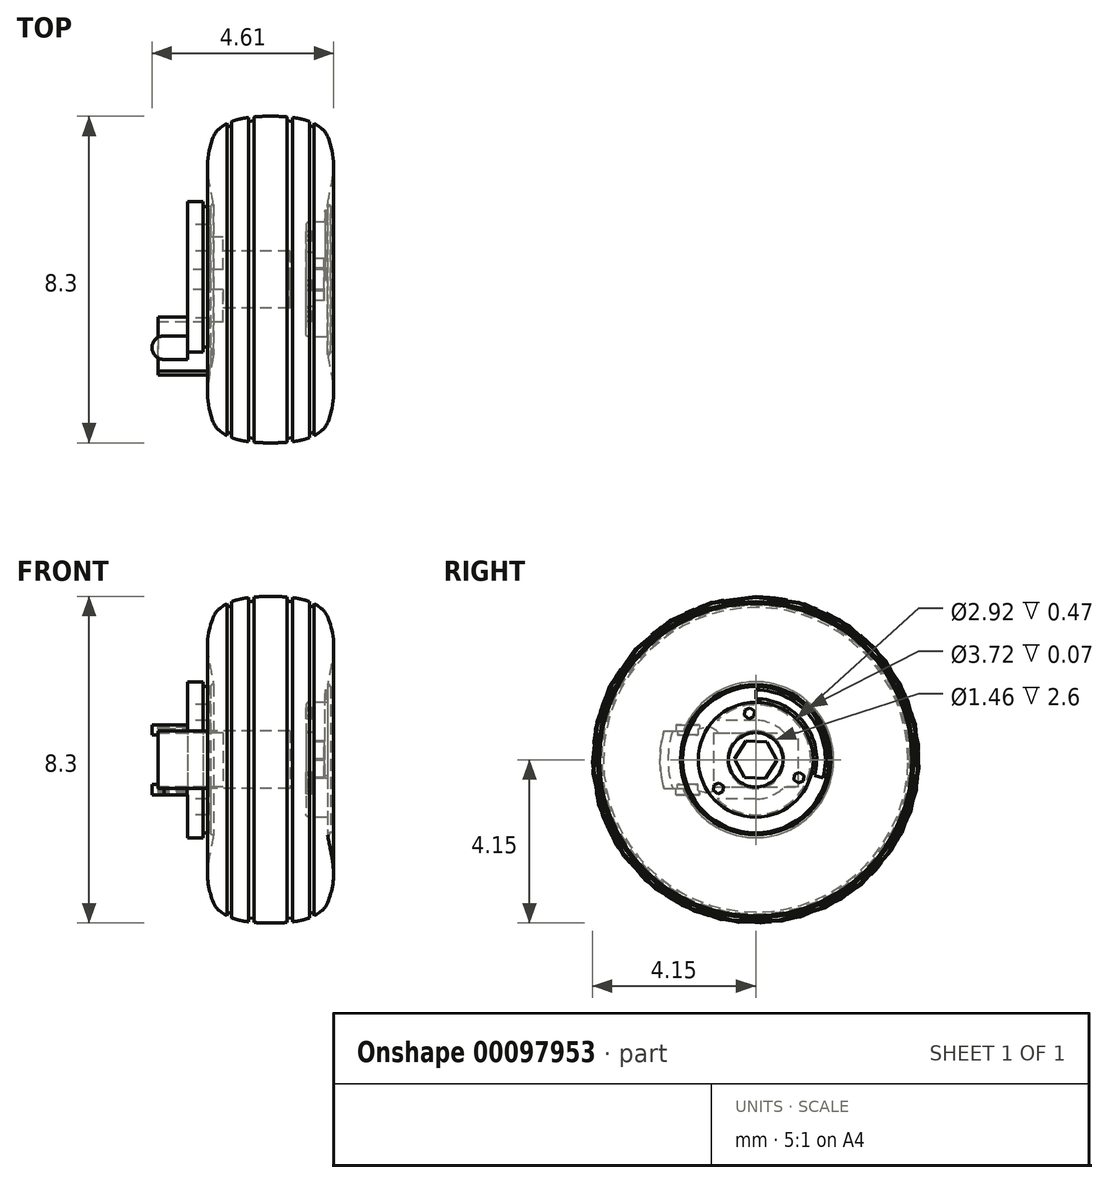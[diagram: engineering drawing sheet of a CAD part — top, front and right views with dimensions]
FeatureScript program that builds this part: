
annotation { "Feature Type Name" : "Feature", "Feature Type Description" : "" }
export const myFeature = defineFeature(function(context is Context, id is Id, definition is map)
    precondition{}
    {
        {
            var Q0;
            Q0=qCreatedBy(makeId("Front.planeOp"),FACE);
            var sketch = newSketch(context, id + "F0", { "sketchPlane" : qUnion([Q0])});
            skLineSegment(sketch, "E0.bottom", {"start": v(0, 0) * mm, "end": v(1.1, 0) * mm});
            skLineSegment(sketch, "E0.top", {"start": v(0.98, 0.7) * mm, "end": v(1.1, 0.7) * mm});
            skLineSegment(sketch, "E0.right", {"start": v(1.11, 0) * mm, "end": v(1.11, 0.7) * mm});
            skLineSegment(sketch, "E1", {"start": v(0.9, 0.77) * mm, "end": v(0.9, 1.38) * mm});
            skLineSegment(sketch, "E2", {"start": v(0.98, 1.46) * mm, "end": v(1.27, 1.46) * mm});
            skLineSegment(sketch, "E3", {"start": v(1.45, 1.64) * mm, "end": v(1.45, 1.86) * mm});
            skLineSegment(sketch, "E4", {"start": v(1.45, 1.91) * mm, "end": v(1.45, 1.91) * mm});
            skLineSegment(sketch, "E5", {"start": v(1.52, 1.91) * mm, "end": v(1.52, 1.91) * mm});
            skLineSegment(sketch, "E6", {"start": v(1.47, 1.91) * mm, "end": v(1.45, 1.91) * mm});
            skPoint(sketch, "E7.orphan", {"position": v(0, 1.46) * mm});
            skPoint(sketch, "E8.visualSharp", {"position": v(1.45, 1.46) * mm});
            skPoint(sketch, "E9.visualSharp", {"position": v(0.9, 1.46) * mm});
            skArc(sketch, "E9.filletArc", {"start": v(0.98, 1.46) * mm, "mid": v(0.92, 1.44) * mm, "end": v(0.9, 1.38) * mm});
            skArc(sketch, "E10.filletArc", {"start": v(0.9, 0.77) * mm, "mid": v(0.92, 0.71) * mm, "end": v(0.98, 0.7) * mm});
            skPoint(sketch, "E11.visualSharp", {"position": v(1.52, 1.91) * mm});
            skArc(sketch, "E11.filletArc", {"start": v(1.52, 1.86) * mm, "mid": v(1.5, 1.9) * mm, "end": v(1.47, 1.91) * mm});
            skLineSegment(sketch, "E12", {"start": v(-0.76, 4.15) * mm, "end": v(0, 4.15) * mm, "construction": true});
            skLineSegment(sketch, "E13", {"start": v(1.6, 4.08) * mm, "end": v(1.6, 0.98) * mm, "construction": true});
            skFitSpline(sketch, "E14", {"points": [v(0, 4.15) * mm, v(1.28, 3.85) * mm, v(1.4, 3.73) * mm, v(1.6, 2.99) * mm, v(1.45, 1.91) * mm], "startDerivative": vector(8.32, 0) * mm, "endDerivative": vector(-0.59, -3.7) * mm});
            skLineSegment(sketch, "E15", {"start": v(0, 4.15) * mm, "end": v(1.72, 4.15) * mm, "construction": true});
            skLineSegment(sketch, "E16", {"start": v(0.42, 4.03) * mm, "end": v(0.56, 4.02) * mm});
            skLineSegment(sketch, "E17", {"start": v(0.99, 3.92) * mm, "end": v(1.1, 3.87) * mm});
            skLineSegment(sketch, "E18", {"start": v(0.42, 4.03) * mm, "end": v(0.42, 4.13) * mm});
            skLineSegment(sketch, "E19", {"start": v(0.56, 4.02) * mm, "end": v(0.56, 4.12) * mm});
            skLineSegment(sketch, "E20", {"start": v(0.99, 3.92) * mm, "end": v(0.99, 4.02) * mm});
            skLineSegment(sketch, "E21", {"start": v(1.1, 3.87) * mm, "end": v(1.1, 3.97) * mm});
            skLineSegment(sketch, "E22", {"start": v(1.52, 1.86) * mm, "end": v(1.45, 1.86) * mm});
            skLineSegment(sketch, "E23", {"start": v(1.27, 1.46) * mm, "end": v(1.45, 1.46) * mm});
            skLineSegment(sketch, "E24", {"start": v(1.45, 1.46) * mm, "end": v(1.45, 1.64) * mm});
            skLineSegment(sketch, "E25.MirrorCS", {"start": v(-1.11, 0) * mm, "end": v(-1.11, 0.7) * mm, "construction": true});
            skLineSegment(sketch, "E26.MirrorCS", {"start": v(-0.98, 0.7) * mm, "end": v(-1.1, 0.7) * mm, "construction": true});
            skArc(sketch, "E27.MirrorCS", {"start": v(-0.9, 0.77) * mm, "mid": v(-0.92, 0.71) * mm, "end": v(-0.98, 0.7) * mm, "construction": true});
            skLineSegment(sketch, "E28.MirrorCS", {"start": v(-0.9, 0.77) * mm, "end": v(-0.9, 1.38) * mm, "construction": true});
            skArc(sketch, "E29.MirrorCS", {"start": v(-1.52, 1.86) * mm, "mid": v(-1.5, 1.9) * mm, "end": v(-1.47, 1.91) * mm});
            skLineSegment(sketch, "E30.MirrorCS", {"start": v(-1.47, 1.91) * mm, "end": v(-1.45, 1.91) * mm});
            skLineSegment(sketch, "E31", {"start": v(-2.1, 1.98) * mm, "end": v(-2.1, 1.4) * mm});
            skLineSegment(sketch, "E32", {"start": v(-2.1, 1.98) * mm, "end": v(-1.71, 1.98) * mm});
            skLineSegment(sketch, "E33", {"start": v(-2.1, 1.4) * mm, "end": v(-1.61, 1.4) * mm});
            skPoint(sketch, "E34.orphan", {"position": v(-2.1, 0.82) * mm});
            skLineSegment(sketch, "E35", {"start": v(-1.61, 0.73) * mm, "end": v(0.49, 0.73) * mm});
            skLineSegment(sketch, "E36", {"start": v(0.49, 0) * mm, "end": v(0.49, 0.96) * mm});
            skLineSegment(sketch, "E37", {"start": v(-0.97, 1.4) * mm, "end": v(-0.97, 0.96) * mm, "construction": true});
            skLineSegment(sketch, "E38", {"start": v(-1.71, 1.98) * mm, "end": v(-1.71, 1.86) * mm});
            skLineSegment(sketch, "E39", {"start": v(-1.52, 1.86) * mm, "end": v(-1.71, 1.86) * mm});
            skLineSegment(sketch, "E40", {"start": v(-2.64, 1.27) * mm, "end": v(-2.64, -0.73) * mm, "construction": true});
            skLineSegment(sketch, "E41", {"start": v(-1.61, 1.4) * mm, "end": v(-1.61, 0.73) * mm});
            skPoint(sketch, "E42.orphan", {"position": v(0, 0.73) * mm});
            skLineSegment(sketch, "E43", {"start": v(-1.61, 1.4) * mm, "end": v(-0.97, 1.4) * mm, "construction": true});
            skLineSegment(sketch, "E44", {"start": v(0, 0.73) * mm, "end": v(0, 5.2) * mm, "construction": true});
            skLineSegment(sketch, "E45.MirrorCS", {"start": v(-1.1, 3.87) * mm, "end": v(-1.1, 3.97) * mm});
            skLineSegment(sketch, "E46.MirrorCS", {"start": v(-0.99, 3.92) * mm, "end": v(-1.1, 3.87) * mm});
            skLineSegment(sketch, "E47.MirrorCS", {"start": v(-0.99, 3.92) * mm, "end": v(-0.99, 4.02) * mm});
            skFitSpline(sketch, "E48.MirrorCS", {"points": [v(0, 4.15) * mm, v(-1.28, 3.85) * mm, v(-1.4, 3.73) * mm, v(-1.6, 2.99) * mm, v(-1.45, 1.91) * mm], "startDerivative": vector(-8.32, 0) * mm, "endDerivative": vector(0.59, -3.7) * mm});
            skLineSegment(sketch, "E49.MirrorCS", {"start": v(-0.42, 4.03) * mm, "end": v(-0.56, 4.02) * mm});
            skLineSegment(sketch, "E50.MirrorCS", {"start": v(-0.42, 4.03) * mm, "end": v(-0.42, 4.13) * mm});
            skLineSegment(sketch, "E51.MirrorCS", {"start": v(-0.56, 4.02) * mm, "end": v(-0.56, 4.12) * mm});
            skLineSegment(sketch, "E52.MirrorCS", {"start": v(-1.52, 1.91) * mm, "end": v(-1.52, 1.91) * mm});
            skFitSpline(sketch, "E53.MirrorCS", {"points": [v(0, 4.15) * mm, v(-1.28, 3.85) * mm, v(-1.4, 3.73) * mm, v(-1.6, 2.99) * mm, v(-1.45, 1.91) * mm], "startDerivative": vector(-8.32, 0) * mm, "endDerivative": vector(0.59, -3.7) * mm});
            skSolve(sketch);
        }
        {
            var Q0;
            Q0=makeQuery(id+"F0.imprint","IMPRINT",FACE,{"disambiguationData":[TD([[makeQuery(id+"F0.imprint","IMPRINT",EDGE,{"derivedFrom":sQuery(id+"F0.wireOp",EDGE,"E0.top")}),-1.0]])]});
            var Q1;
            Q1=sQuery(id+"F0.wireOp",EDGE,"E25.MirrorCS");
            var Q2;
            Q2=sQuery(id+"F0.wireOp",EDGE,"E28.MirrorCS");
            var Q3;
            Q3=sQuery(id+"F0.wireOp",EDGE,"E27.MirrorCS");
            var Q4;
            Q4=sQuery(id+"F0.wireOp",EDGE,"E26.MirrorCS");
            var Q5;
            Q5=sQuery(id+"F0.wireOp",EDGE,"E0.bottom");
            revolve(context, id + "F1", {"entities" : qUnion([Q0]), "surfaceEntities" : qUnion([Q1, Q2, Q3, Q4]), "axis" : qUnion([Q5]), "revolveType" : RevolveType.FULL});
        }
        {
            var Q0;
            Q0=makeQuery(id+"F1.opRevolve","SWEPT_FACE",FACE,{"disambiguationData":[OSD([sQuery(id+"F0.wireOp",EDGE,"E31")])]});
            var sketch = newSketch(context, id + "F2", { "sketchPlane" : qUnion([Q0])});
            skArc(sketch, "E54", {"start": v(0, 1) * mm, "mid": v(-1, 0) * mm, "end": v(0, -1) * mm});
            skLineSegment(sketch, "E55", {"start": v(0, 1) * mm, "end": v(0.98, 1) * mm});
            skLineSegment(sketch, "E56", {"start": v(0, -1) * mm, "end": v(0.98, -1) * mm});
            skArc(sketch, "E57", {"start": v(0.98, -1) * mm, "mid": v(1.4, 0) * mm, "end": v(0.98, 1) * mm});
            skCircle(sketch, "E58", {"center": v(0, 0) * mm, "radius": 0.73 * mm});
            skSolve(sketch);
        }
        {
            var Q0;
            Q0=qSketchRegion(id+"F2",true);
            var Q1;
            Q1=makeQuery(id+"F1.opRevolve","SWEPT_FACE",FACE,{"disambiguationData":[OSD([sQuery(id+"F0.wireOp",EDGE,"E41")])]});
            extrude(context, id + "F3", {"entities" : qUnion([Q0]), "operationType" : NewBodyOperationType.ADD, "endBound" : BoundingType.UP_TO_SURFACE, "oppositeDirection" : true, "endBoundEntityFace" : qUnion([Q1]), "depth" : 25 * mm});
        }
        {
            var Q0;
            Q0=makeQuery(id+"F3.boolean.opBoolean","MERGE",FACE,{"derivedFrom":[makeQuery(id+"F1.opRevolve","SWEPT_FACE",FACE,{"disambiguationData":[OSD([sQuery(id+"F0.wireOp",EDGE,"E31")])]}),makeQuery(id+"F3.opExtrude","CAP_FACE",FACE,{"disambiguationData":[OSD([sQuery(id+"F2.wireOp",EDGE,"E54"),sQuery(id+"F2.wireOp",EDGE,"E55"),sQuery(id+"F2.wireOp",EDGE,"E56"),sQuery(id+"F2.wireOp",EDGE,"E58"),sQuery(id+"F2.wireOp",EDGE,"E57")])],"isStart":true})]});
            var sketch = newSketch(context, id + "F4", { "sketchPlane" : qUnion([Q0])});
            skLineSegment(sketch, "E59.bottom", {"start": v(1.08, 0.68) * mm, "end": v(-1.08, 0.69) * mm});
            skLineSegment(sketch, "E59.top", {"start": v(1.08, -0.69) * mm, "end": v(-1.08, -0.68) * mm});
            skLineSegment(sketch, "E59.left", {"start": v(1.08, 0.68) * mm, "end": v(1.08, -0.69) * mm});
            skLineSegment(sketch, "E59.right", {"start": v(-1.08, 0.69) * mm, "end": v(-1.08, -0.68) * mm});
            skPoint(sketch, "E59.middle", {"position": v(0, 0) * mm});
            skSolve(sketch);
        }
        {
            var Q0;
            Q0=qSketchRegion(id+"F4",true);
            extrude(context, id + "F5", {"entities" : qUnion([Q0]), "operationType" : NewBodyOperationType.REMOVE, "oppositeDirection" : true, "depth" : 0.9 * mm});
        }
        {
            var Q0;
            Q0=makeQuery(id+"F3.boolean.opBoolean","MERGE",FACE,{"derivedFrom":[makeQuery(id+"F1.opRevolve","SWEPT_FACE",FACE,{"disambiguationData":[OSD([sQuery(id+"F0.wireOp",EDGE,"E31")])]}),makeQuery(id+"F3.opExtrude","CAP_FACE",FACE,{"disambiguationData":[OSD([sQuery(id+"F2.wireOp",EDGE,"E54"),sQuery(id+"F2.wireOp",EDGE,"E55"),sQuery(id+"F2.wireOp",EDGE,"E56"),sQuery(id+"F2.wireOp",EDGE,"E58"),sQuery(id+"F2.wireOp",EDGE,"E57")])],"isStart":true})]});
            var sketch = newSketch(context, id + "F6", { "sketchPlane" : qUnion([Q0])});
            skLineSegment(sketch, "E60", {"start": v(2.33, 0.73) * mm, "end": v(2.33, -0.73) * mm, "construction": true});
            skLineSegment(sketch, "E61", {"start": v(0, 0) * mm, "end": v(2.43, 0) * mm, "construction": true});
            skArc(sketch, "E62", {"start": v(2.43, 0) * mm, "mid": v(2.4, 0.37) * mm, "end": v(2.33, 0.73) * mm});
            skLineSegment(sketch, "E63", {"start": v(2.33, 0.73) * mm, "end": v(1.68, 0.73) * mm});
            skLineSegment(sketch, "E64", {"start": v(2.65, 0.83) * mm, "end": v(-0.85, 0.83) * mm, "construction": true});
            skLineSegment(sketch, "E65", {"start": v(0.89, 2.3) * mm, "end": v(0.9, -2.15) * mm, "construction": true});
            skLineSegment(sketch, "E66", {"start": v(1.23, 1.18) * mm, "end": v(1.23, 0.25) * mm, "construction": true});
            skLineSegment(sketch, "E67", {"start": v(1.57, 0.49) * mm, "end": v(0.7, 0.49) * mm, "construction": true});
            skArc(sketch, "E68", {"start": v(1.31, 0.82) * mm, "mid": v(1.11, 0.8) * mm, "end": v(0.95, 0.68) * mm});
            skLineSegment(sketch, "E69", {"start": v(1.68, 0.73) * mm, "end": v(1.27, 0.83) * mm});
            skLineSegment(sketch, "E70", {"start": v(0.95, 0.68) * mm, "end": v(1.08, 0.68) * mm});
            skLineSegment(sketch, "E71", {"start": v(1.08, 0.68) * mm, "end": v(1.08, 0) * mm});
            skLineSegment(sketch, "E72", {"start": v(1.08, 0) * mm, "end": v(2.43, 0) * mm});
            skArc(sketch, "E73.MirrorCS", {"start": v(2.43, 0) * mm, "mid": v(2.4, -0.37) * mm, "end": v(2.33, -0.73) * mm});
            skLineSegment(sketch, "E74.MirrorCS", {"start": v(2.33, -0.73) * mm, "end": v(1.68, -0.73) * mm});
            skLineSegment(sketch, "E75.MirrorCS", {"start": v(1.68, -0.73) * mm, "end": v(1.27, -0.83) * mm});
            skArc(sketch, "E76.MirrorCS", {"start": v(1.31, -0.82) * mm, "mid": v(1.11, -0.8) * mm, "end": v(0.95, -0.68) * mm});
            skLineSegment(sketch, "E77.MirrorCS", {"start": v(0.95, -0.68) * mm, "end": v(1.08, -0.68) * mm});
            skLineSegment(sketch, "E78.MirrorCS", {"start": v(1.08, -0.68) * mm, "end": v(1.08, 0) * mm});
            skSolve(sketch);
        }
        {
            var Q0;
            Q0=qSketchRegion(id+"F6",true);
            extrude(context, id + "F7", {"entities" : qUnion([Q0]), "operationType" : NewBodyOperationType.ADD, "depth" : 0.75 * mm, "hasSecondDirection" : true, "secondDirectionOppositeDirection" : true, "secondDirectionDepth" : 0.6 * mm});
        }
        {
            var Q0;
            Q0=makeQuery(id+"F7.opExtrude","SWEPT_FACE",FACE,{"disambiguationData":[OSD([sQuery(id+"F6.wireOp",EDGE,"E63")])]});
            var sketch = newSketch(context, id + "F8", { "sketchPlane" : qUnion([Q0])});
            skLineSegment(sketch, "E79", {"start": v(-2.7, -1.43) * mm, "end": v(-2.7, -2.03) * mm, "construction": true});
            skArc(sketch, "E80", {"start": v(-2.7, -1.43) * mm, "mid": v(-3, -1.73) * mm, "end": v(-2.7, -2.03) * mm});
            skLineSegment(sketch, "E81", {"start": v(-2.1, -2.03) * mm, "end": v(-2.1, -1.43) * mm});
            skLineSegment(sketch, "E82", {"start": v(-2.7, -1.43) * mm, "end": v(-2.1, -1.43) * mm});
            skLineSegment(sketch, "E83", {"start": v(-2.7, -2.03) * mm, "end": v(-2.1, -2.03) * mm});
            skSolve(sketch);
        }
        {
            var Q0;
            Q0=qSketchRegion(id+"F8",true);
            extrude(context, id + "F9", {"entities" : qUnion([Q0]), "operationType" : NewBodyOperationType.ADD, "depth" : 0.16 * mm, "hasSecondDirection" : true, "secondDirectionOppositeDirection" : true, "secondDirectionDepth" : 0.1 * mm});
        }
        {
            var Q0;
            Q0=makeQuery(id+"F7.opExtrude","SWEPT_FACE",FACE,{"disambiguationData":[OSD([sQuery(id+"F6.wireOp",EDGE,"E74.MirrorCS")])]});
            var sketch = newSketch(context, id + "F10", { "sketchPlane" : qUnion([Q0])});
            skArc(sketch, "E84", {"start": v(-2.7, 2.03) * mm, "mid": v(-3.01, 1.73) * mm, "end": v(-2.7, 1.43) * mm});
            skLineSegment(sketch, "E85", {"start": v(-2.7, 1.43) * mm, "end": v(-2.12, 1.43) * mm});
            skLineSegment(sketch, "E86", {"start": v(-2.12, 1.43) * mm, "end": v(-2.12, 2.03) * mm});
            skLineSegment(sketch, "E87", {"start": v(-2.72, 2.03) * mm, "end": v(-2.12, 2.03) * mm});
            skSolve(sketch);
        }
        {
            var Q0;
            Q0=qSketchRegion(id+"F10",true);
            extrude(context, id + "F11", {"entities" : qUnion([Q0]), "operationType" : NewBodyOperationType.ADD, "depth" : 0.16 * mm, "hasSecondDirection" : true, "secondDirectionOppositeDirection" : true, "secondDirectionDepth" : 0.1 * mm});
        }
        {
            var Q0;
            Q0=makeQuery(id+"F1.opRevolve","SWEPT_FACE",FACE,{"disambiguationData":[OSD([sQuery(id+"F0.wireOp",EDGE,"E0.right")])]});
            var sketch = newSketch(context, id + "F12", { "sketchPlane" : qUnion([Q0])});
            skCircle(sketch, "E88.cCircle", {"center": v(0, 0) * mm, "radius": 0.47 * mm, "construction": true});
            skLineSegment(sketch, "E88.0", {"start": v(0.29, 0.45) * mm, "end": v(0.54, -0.02) * mm});
            skLineSegment(sketch, "E88.1", {"start": v(0.54, -0.02) * mm, "end": v(0.25, -0.48) * mm});
            skLineSegment(sketch, "E88.2", {"start": v(0.25, -0.48) * mm, "end": v(-0.29, -0.45) * mm});
            skLineSegment(sketch, "E88.3", {"start": v(-0.29, -0.45) * mm, "end": v(-0.54, 0.02) * mm});
            skLineSegment(sketch, "E88.4", {"start": v(-0.54, 0.02) * mm, "end": v(-0.25, 0.48) * mm});
            skLineSegment(sketch, "E88.5", {"start": v(-0.25, 0.48) * mm, "end": v(0.29, 0.45) * mm});
            skPoint(sketch, "E88.0.midPoint", {"position": v(0.41, 0.22) * mm});
            skSolve(sketch);
        }
        {
            var Q0;
            Q0=qSketchRegion(id+"F12",true);
            extrude(context, id + "F13", {"entities" : qUnion([Q0]), "operationType" : NewBodyOperationType.ADD, "depth" : 0.25 * mm});
        }
        {
            var Q0;
            Q0=makeQuery(id+"F1.opRevolve","SWEPT_FACE",FACE,{"disambiguationData":[OSD([sQuery(id+"F0.wireOp",EDGE,"E1")])]});
            var sketch = newSketch(context, id + "F14", { "sketchPlane" : qUnion([Q0])});
            skPoint(sketch, "E89.center", {"position": v(0, 0) * mm});
            skCircle(sketch, "E90.cCircle", {"center": v(-0.16, 1.18) * mm, "radius": 0.12 * mm, "construction": true});
            skLineSegment(sketch, "E90.0", {"start": v(-0.28, 1.12) * mm, "end": v(-0.27, 1.26) * mm});
            skLineSegment(sketch, "E90.1", {"start": v(-0.27, 1.26) * mm, "end": v(-0.14, 1.32) * mm});
            skLineSegment(sketch, "E90.2", {"start": v(-0.14, 1.32) * mm, "end": v(-0.03, 1.24) * mm});
            skLineSegment(sketch, "E90.3", {"start": v(-0.03, 1.24) * mm, "end": v(-0.04, 1.1) * mm});
            skLineSegment(sketch, "E90.4", {"start": v(-0.04, 1.1) * mm, "end": v(-0.17, 1.04) * mm});
            skLineSegment(sketch, "E90.5", {"start": v(-0.17, 1.04) * mm, "end": v(-0.28, 1.12) * mm});
            skPoint(sketch, "E90.0.midPoint", {"position": v(-0.27, 1.19) * mm});
            skLineSegment(sketch, "E91", {"start": v(0, 0) * mm, "end": v(-0.16, 1.18) * mm, "construction": true});
            skLineSegment(sketch, "E92.1.0", {"start": v(-0.83, -0.8) * mm, "end": v(-0.96, -0.86) * mm});
            skLineSegment(sketch, "E92.1.1", {"start": v(-0.96, -0.86) * mm, "end": v(-1.07, -0.78) * mm});
            skLineSegment(sketch, "E92.1.2", {"start": v(-1.07, -0.78) * mm, "end": v(-1.06, -0.65) * mm});
            skLineSegment(sketch, "E92.1.3", {"start": v(-1.06, -0.65) * mm, "end": v(-0.93, -0.59) * mm});
            skLineSegment(sketch, "E92.1.4", {"start": v(-0.93, -0.59) * mm, "end": v(-0.82, -0.67) * mm});
            skLineSegment(sketch, "E92.1.5", {"start": v(-0.82, -0.67) * mm, "end": v(-0.83, -0.8) * mm});
            skCircle(sketch, "E92.1.6", {"center": v(-0.94, -0.72) * mm, "radius": 0.12 * mm, "construction": true});
            skLineSegment(sketch, "E92.2.0", {"start": v(1.11, -0.32) * mm, "end": v(1.22, -0.4) * mm});
            skLineSegment(sketch, "E92.2.1", {"start": v(1.22, -0.4) * mm, "end": v(1.21, -0.53) * mm});
            skLineSegment(sketch, "E92.2.2", {"start": v(1.21, -0.53) * mm, "end": v(1.09, -0.6) * mm});
            skLineSegment(sketch, "E92.2.3", {"start": v(1.09, -0.6) * mm, "end": v(0.97, -0.51) * mm});
            skLineSegment(sketch, "E92.2.4", {"start": v(0.97, -0.51) * mm, "end": v(0.99, -0.38) * mm});
            skLineSegment(sketch, "E92.2.5", {"start": v(0.99, -0.38) * mm, "end": v(1.11, -0.32) * mm});
            skCircle(sketch, "E92.2.6", {"center": v(1.1, -0.46) * mm, "radius": 0.12 * mm, "construction": true});
            skSolve(sketch);
        }
        {
            var Q0;
            Q0=qSketchRegion(id+"F14",true);
            extrude(context, id + "F15", {"entities" : qUnion([Q0]), "operationType" : NewBodyOperationType.ADD, "depth" : 0.15 * mm});
        }
        {
            var Q0;
            Q0=qCreatedBy(makeId("Front.planeOp"),FACE);
            var sketch = newSketch(context, id + "F16", { "sketchPlane" : qUnion([Q0])});
            skLineSegment(sketch, "E93.bottom", {"start": v(1.39, 1.77) * mm, "end": v(1.6, 1.77) * mm});
            skLineSegment(sketch, "E93.top", {"start": v(1.4, 1.55) * mm, "end": v(1.6, 1.55) * mm});
            skLineSegment(sketch, "E93.left", {"start": v(1.4, 1.77) * mm, "end": v(1.4, 1.55) * mm});
            skLineSegment(sketch, "E93.right", {"start": v(1.6, 1.77) * mm, "end": v(1.6, 1.55) * mm});
            skLineSegment(sketch, "E94", {"start": v(0, 0) * mm, "end": v(2.72, 0) * mm, "construction": true});
            skSolve(sketch);
        }
        {
            var Q0;
            Q0=qSketchRegion(id+"F16",true);
            var Q1;
            Q1=sQuery(id+"F16.wireOp",EDGE,"E94");
            revolve(context, id + "F17", {"operationType" : NewBodyOperationType.REMOVE, "entities" : qUnion([Q0]), "axis" : qUnion([Q1]), "revolveType" : RevolveType.ONE_DIRECTION, "oppositeDirection" : true, "angle" : 105 * degree});
        }
    });
